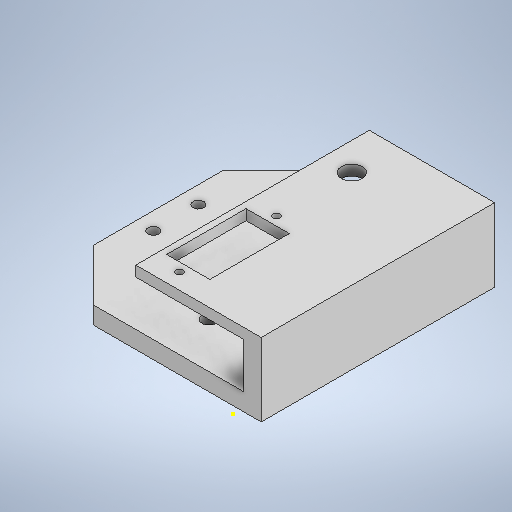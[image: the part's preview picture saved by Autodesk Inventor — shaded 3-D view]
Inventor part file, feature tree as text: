
AUTODESK INVENTOR PART (.ipt)
format: ipt  version: 2025.1 (Build 291241020, 241B)  size: 480,768 bytes
history: native  units: in
note: dims shown in document units (in); Inventor stores cm internally (conversion verified against a paired STEP export)
features: sketch x25, extrude x24
ambient origin geometry x8: Origin, YZ Plane, XZ Plane, XY Plane, X Axis, Y Axis, Z Axis, Center Point
bodies: Solid2 (feature_tree), Solid1 (feature_tree)
feature tree (49):
  extrude  "Extrusion1"  Depth=0.3937in
  extrude  "Extrusion2"  Depth=0.3937in TaperAngle=0.0deg
  extrude  "Extrusion3"  Depth=0.3937in TaperAngle=0.0deg
  extrude  "Extrusion4"  Depth=0.1181in
  extrude  "Extrusion5"  Depth=0.3937in TaperAngle=0.0deg
  extrude  "Extrusion6"  Depth=0.7087in
  extrude  "Extrusion7"  Depth=0.748in
  extrude  "Extrusion8"  Depth=2.3937in TaperAngle=0.0deg
  extrude  "Extrusion9"  Depth=0.3937in TaperAngle=0.0deg
  extrude  "Extrusion10"  TaperAngle=90.0deg  [1 undecoded]
  extrude  "Extrusion11"  Depth=0.5906in
  extrude  "Extrusion12"  Depth=0.3937in TaperAngle=0.0deg
  extrude  "Extrusion13"  Depth=0.1969in
  extrude  "Extrusion14"  Depth=0.1969in
  extrude  "Extrusion15"  Depth=1.0651in
  extrude  "Extrusion16"  Depth=0.122in
  extrude  "Extrusion17"  Depth=0.3937in TaperAngle=0.0deg
  sketch  "Sketch18"  dims[d48=0.3937in d49=0.0in d50=0.3937in d51=0.0in]
  extrude  "Extrusion18"  Depth=0.3937in TaperAngle=0.0deg
  extrude  "Extrusion19"  Depth=0.0787in
  extrude  "Extrusion20"  Depth=2.7313in TaperAngle=0.0deg
  extrude  "Extrusion21"  Depth=0.3937in
  extrude  "Extrusion22"  Depth=0.3937in
  extrude  "Extrusion23"  Depth=0.5906in
  extrude  "Extrusion26"  Depth=0.3937in TaperAngle=0.0deg
  sketch  "Sketch1"  dims[d0=0.3937in d1=0.0in d2=1.0945in]
  sketch  "Sketch2"  dims[d3=0.0787in d4=0.3937in d5=0.0in]
  sketch  "Sketch3"  dims[d6=0.0984in d7=0.3937in d8=0.0in]
  sketch  "Sketch4"  dims[d9=0.2362in d10=0.1181in]
  sketch  "Sketch5"  dims[d11=0.3937in d12=0.0in d13=2.3937in d14=0.0in]
  sketch  "Sketch6"  dims[d15=2.3937in d16=0.0in d17=0.7087in]
  sketch  "Sketch7"  dims[d18=0.1575in d19=0.748in]
  sketch  "Sketch8"  dims[d20=0.122in d21=2.3937in d22=0.0in]
  sketch  "Sketch9"  dims[d23=2.3937in d24=0.0in d25=0.3937in d26=0.0in]
  sketch  "Sketch10"  dims[d27=0.5118in d28=90.0deg]
  sketch  "Sketch11"  dims[d29=6.7687in d30=0.0in d31=0.5906in]
  sketch  "Sketch12"  dims[d32=6.7687in d33=0.0in d34=0.3937in d35=0.0in]
  sketch  "Sketch13"  dims[d36=0.3937in d37=0.1969in]
  sketch  "Sketch14"  dims[d38=0.3937in d39=0.0in d40=0.1969in]
  sketch  "Sketch15"  dims[d41=90.0deg d42=1.0651in]
  sketch  "Sketch16"  dims[d43=1.0651in d44=0.122in]
  sketch  "Sketch17"  dims[d45=0.122in d46=0.3937in d47=0.0in]
  sketch  "Sketch19"  dims[d52=0.3937in d53=0.0in d54=0.0787in]
  sketch  "Sketch20"  dims[d55=2.7313in d56=0.0in d57=2.7313in d58=0.0in]
  sketch  "Sketch21"  dims[d59=0.3937in d60=0.0in d61=0.2362in]
  sketch  "Sketch22"  dims[d62=0.3937in d63=0.0in d64=0.5906in]
  sketch  "Sketch23"  dims[d65=0.5906in d66=0.5906in]
  sketch  "Sketch24"  dims[d67=0.5906in d68=0.3937in d69=0.0in]
  sketch  "Sketch27"  dims[d70=0.1142in d71=0.0in d76=0.0787in d77=0.0in]
note: 1 required parameter value undecoded (feature->parameter linkage not recoverable at this tier; creation-order binding heuristic only, values carry confidence <= 0.55)
